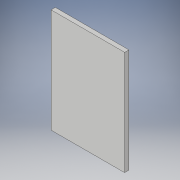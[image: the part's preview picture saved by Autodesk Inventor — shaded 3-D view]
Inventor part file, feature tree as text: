
AUTODESK INVENTOR PART (.ipt)
format: ipt  version: 2019 (Build 230136000, 136)  size: 92,672 bytes
history: native  units: in
note: dims shown in document units (in); Inventor stores cm internally (conversion verified against a paired STEP export)
features: extrude x1, sketch x1
ambient origin geometry x8: Origin, YZ Plane, XZ Plane, XY Plane, X Axis, Y Axis, Z Axis, Center Point
bodies: Solid1 (feature_tree)
feature tree (2):
  extrude  "Extrusion1"  Depth=1.1181in
  sketch  "Sketch1"  dims[d0=1.5835in d1=1.1181in d2=0.0652in d3=0.0in]
